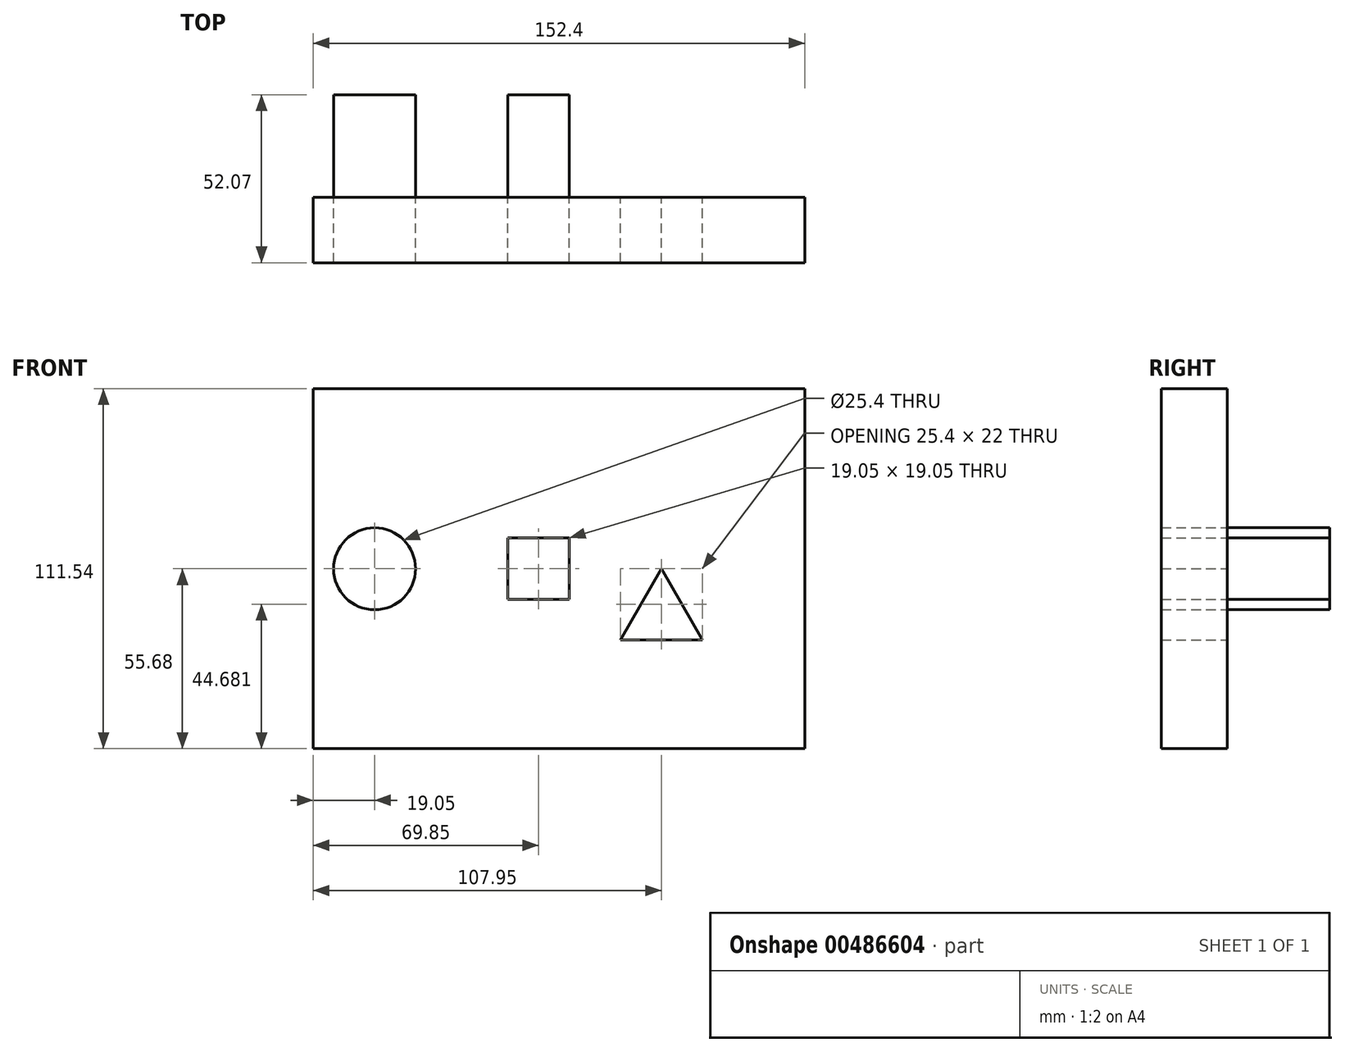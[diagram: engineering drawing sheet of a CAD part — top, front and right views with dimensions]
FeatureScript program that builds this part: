
annotation { "Feature Type Name" : "Feature", "Feature Type Description" : "" }
export const myFeature = defineFeature(function(context is Context, id is Id, definition is map)
    precondition{}
    {
        {
            var Q0;
            Q0=qCreatedBy(makeId("Front.planeOp"),FACE);
            var sketch = newSketch(context, id + "F0", { "sketchPlane" : qUnion([Q0])});
            skLineSegment(sketch, "E0", {"start": v(0, 0) * mm, "end": v(-31.75, 0) * mm});
            skLineSegment(sketch, "E1.bottom", {"start": v(-22.22, 9.52) * mm, "end": v(-41.27, 9.52) * mm});
            skLineSegment(sketch, "E1.top", {"start": v(-22.23, -9.53) * mm, "end": v(-41.27, -9.53) * mm});
            skLineSegment(sketch, "E1.left", {"start": v(-22.22, 9.52) * mm, "end": v(-22.23, -9.53) * mm});
            skLineSegment(sketch, "E1.right", {"start": v(-41.27, 9.52) * mm, "end": v(-41.27, -9.53) * mm});
            skPoint(sketch, "E1.middle", {"position": v(-31.75, 0) * mm});
            skLineSegment(sketch, "E2", {"start": v(-31.75, 0) * mm, "end": v(-82.55, 0) * mm});
            skCircle(sketch, "E3", {"center": v(-82.55, 0) * mm, "radius": 12.7 * mm});
            skLineSegment(sketch, "E4", {"start": v(0, 0) * mm, "end": v(6.35, 0) * mm});
            skLineSegment(sketch, "E5", {"start": v(6.35, -8.11) * mm, "end": v(-6.35, -8.11) * mm});
            skLineSegment(sketch, "E6", {"start": v(6.35, 0) * mm, "end": v(-6.35, -22) * mm});
            skLineSegment(sketch, "E7", {"start": v(-6.35, -22) * mm, "end": v(19.05, -22) * mm});
            skLineSegment(sketch, "E8", {"start": v(6.35, 0) * mm, "end": v(19.05, -22) * mm});
            skLineSegment(sketch, "E9", {"start": v(6.35, 0) * mm, "end": v(50.8, 0) * mm});
            skLineSegment(sketch, "E10.bottom", {"start": v(50.8, 55.86) * mm, "end": v(-101.6, 55.86) * mm});
            skLineSegment(sketch, "E10.top", {"start": v(50.8, -55.68) * mm, "end": v(-101.6, -55.68) * mm});
            skLineSegment(sketch, "E10.left", {"start": v(50.8, 55.86) * mm, "end": v(50.8, -55.68) * mm});
            skLineSegment(sketch, "E10.right", {"start": v(-101.6, 55.86) * mm, "end": v(-101.6, -55.68) * mm});
            skSolve(sketch);
        }
        {
            var Q0;
            {var subQ7=sQuery(id+"F0.wireOp",EDGE,"E1.bottom");Q0=makeQuery(id+"F0.imprint","IMPRINT",FACE,{"disambiguationData":[TD([[makeQuery(id+"F0.imprint","IMPRINT",EDGE,{"derivedFrom":subQ7}),-1.0]])]});}
            extrude(context, id + "F1", {"entities" : qUnion([Q0]), "depth" : 20.32 * mm});
        }
        {
            var Q0;
            Q0=makeQuery(id+"F0.imprint","IMPRINT",FACE,{"disambiguationData":[TD([[makeQuery(id+"F0.imprint","IMPRINT",EDGE,{"derivedFrom":sQuery(id+"F0.wireOp",EDGE,"E3")}),1.0]])]});
            var Q1;
            {var subQ1=sQuery(id+"F0.wireOp",EDGE,"E1.top");Q1=makeQuery(id+"F0.imprint","IMPRINT",FACE,{"disambiguationData":[TD([[makeQuery(id+"F0.imprint","IMPRINT",EDGE,{"derivedFrom":subQ1}),-1.0]])]});}
            var Q2;
            {var subQ1=sQuery(id+"F0.wireOp",EDGE,"E1.bottom");Q2=makeQuery(id+"F0.imprint","IMPRINT",FACE,{"disambiguationData":[TD([[makeQuery(id+"F0.imprint","IMPRINT",EDGE,{"derivedFrom":subQ1}),1.0]])]});}
            extrude(context, id + "F2", {"entities" : qUnion([Q0, Q1, Q2]), "oppositeDirection" : true, "depth" : 31.75 * mm});
        }
        {
            var Q0;
            Q0=makeQuery(id+"F2.opExtrude","CAP_FACE",FACE,{"disambiguationData":[OSD([sQuery(id+"F0.wireOp",EDGE,"E3")])],"isStart":true});
            var Q1;
            Q1=makeQuery(id+"F2.opExtrude","CAP_FACE",FACE,{"disambiguationData":[OSD([sQuery(id+"F0.wireOp",EDGE,"E1.bottom"),sQuery(id+"F0.wireOp",EDGE,"E1.top"),sQuery(id+"F0.wireOp",EDGE,"E1.left"),sQuery(id+"F0.wireOp",EDGE,"E1.right")])],"isStart":true});
            extrude(context, id + "F3", {"entities" : qUnion([Q0, Q1]), "depth" : 20.32 * mm});
        }
    });
